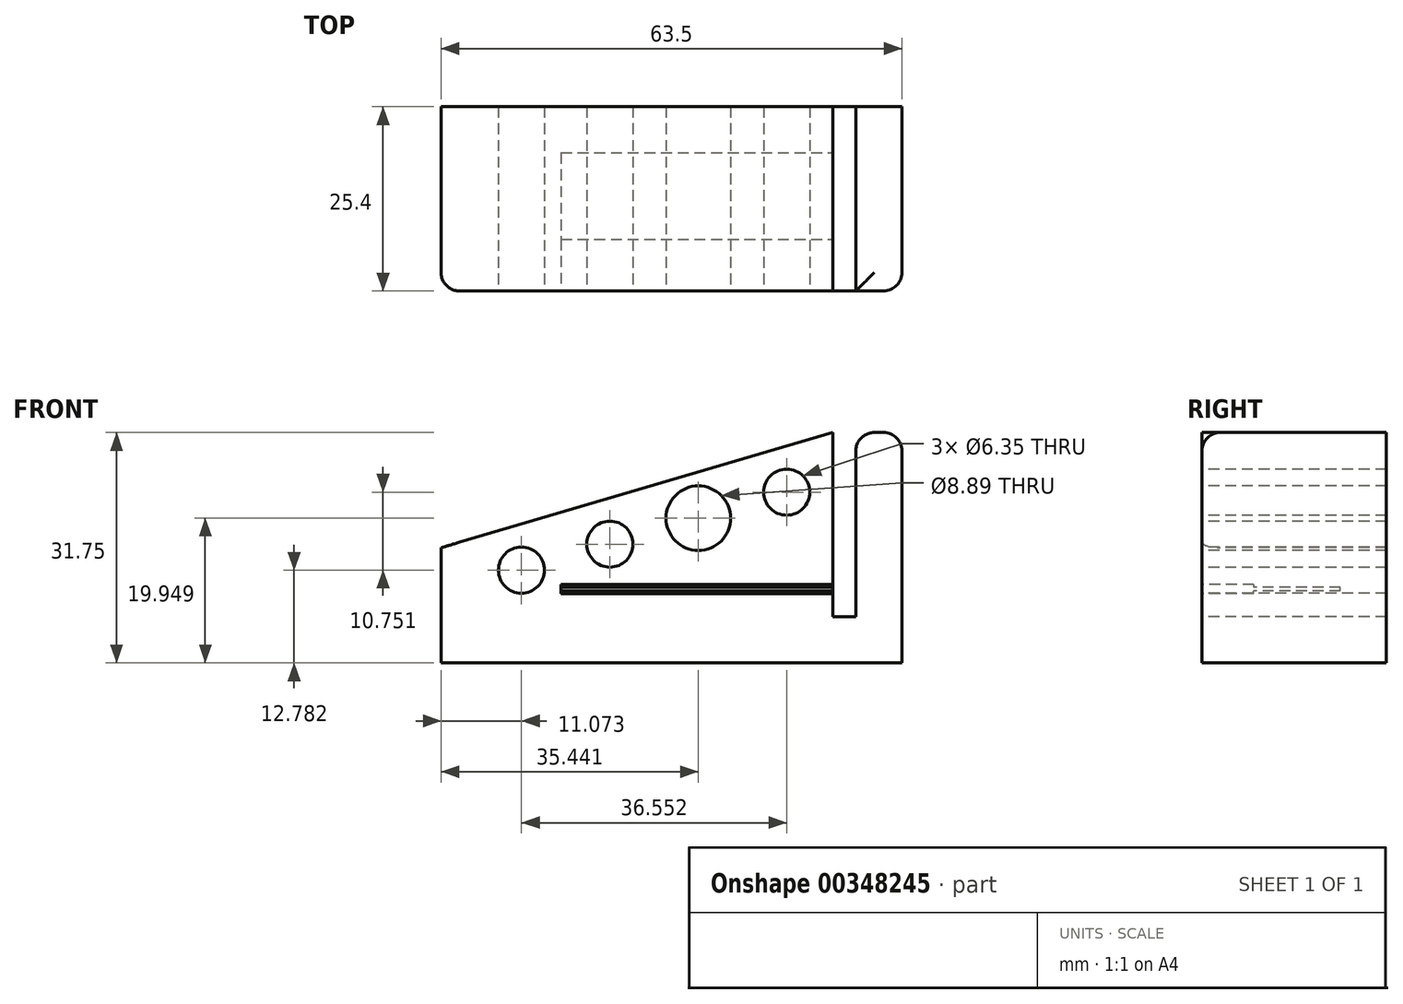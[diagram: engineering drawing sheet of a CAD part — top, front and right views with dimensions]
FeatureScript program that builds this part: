
annotation { "Feature Type Name" : "Feature", "Feature Type Description" : "" }
export const myFeature = defineFeature(function(context is Context, id is Id, definition is map)
    precondition{}
    {
        {
            var Q0;
            Q0=qCreatedBy(makeId("Top.planeOp"),FACE);
            var sketch = newSketch(context, id + "F0", { "sketchPlane" : qUnion([Q0])});
            skLineSegment(sketch, "E0.bottom", {"start": v(-31.75, 12.7) * mm, "end": v(31.75, 12.7) * mm});
            skLineSegment(sketch, "E0.top", {"start": v(-31.75, -12.7) * mm, "end": v(31.75, -12.7) * mm});
            skLineSegment(sketch, "E0.left", {"start": v(-31.75, 12.7) * mm, "end": v(-31.75, -12.7) * mm});
            skLineSegment(sketch, "E0.right", {"start": v(31.75, 12.7) * mm, "end": v(31.75, -12.7) * mm});
            skPoint(sketch, "E0.middle", {"position": v(0, 0) * mm});
            skSolve(sketch);
        }
        {
            var Q0;
            Q0 = qSketchRegion(id + "F0", true);
            extrude(context, id + "F1", {"entities" : qUnion([Q0]), "depth" : 50.8 * mm});
        }
        {
            var Q0;
            Q0=makeQuery(id+"F1.opExtrude","CAP_FACE",FACE,{"disambiguationData":[OSD([sQuery(id+"F0.wireOp",EDGE,"E0.bottom"),sQuery(id+"F0.wireOp",EDGE,"E0.top"),sQuery(id+"F0.wireOp",EDGE,"E0.left"),sQuery(id+"F0.wireOp",EDGE,"E0.right")])],"isStart":false});
            var sketch = newSketch(context, id + "F2", { "sketchPlane" : qUnion([Q0])});
            skLineSegment(sketch, "E1.bottom", {"start": v(22.23, 12.7) * mm, "end": v(25.4, 12.7) * mm});
            skLineSegment(sketch, "E1.top", {"start": v(22.22, -12.7) * mm, "end": v(25.4, -12.7) * mm});
            skLineSegment(sketch, "E1.left", {"start": v(22.22, 12.7) * mm, "end": v(22.22, -12.7) * mm});
            skLineSegment(sketch, "E1.right", {"start": v(25.4, 12.7) * mm, "end": v(25.4, -12.7) * mm});
            skLineSegment(sketch, "E2", {"start": v(23.81, 12.7) * mm, "end": v(22.23, 0) * mm, "construction": true});
            skSolve(sketch);
        }
        {
            var Q0;
            Q0 = qSketchRegion(id + "F2", true);
            extrude(context, id + "F3", {"entities" : qUnion([Q0]), "operationType" : NewBodyOperationType.REMOVE, "oppositeDirection" : true, "depth" : 25.4 * mm});
        }
        {
            var Q0;
            Q0=makeQuery(id+"F1.opExtrude","SWEPT_FACE",FACE,{"disambiguationData":[OSD([sQuery(id+"F0.wireOp",EDGE,"E0.top")])]});
            var sketch = newSketch(context, id + "F4", { "sketchPlane" : qUnion([Q0])});
            skLineSegment(sketch, "E3.bottom", {"start": v(-15.24, 29.85) * mm, "end": v(25.4, 29.85) * mm});
            skLineSegment(sketch, "E3.top", {"start": v(-15.24, 28.58) * mm, "end": v(25.4, 28.58) * mm});
            skLineSegment(sketch, "E3.left", {"start": v(-15.24, 29.84) * mm, "end": v(-15.24, 28.58) * mm});
            skLineSegment(sketch, "E3.right", {"start": v(25.4, 29.84) * mm, "end": v(25.4, 28.58) * mm});
            skLineSegment(sketch, "E4", {"start": v(5.08, 29.84) * mm, "end": v(-15.24, 29.21) * mm, "construction": true});
            skSolve(sketch);
        }
        {
            var Q0;
            Q0 = qSketchRegion(id + "F4", true);
            extrude(context, id + "F5", {"entities" : qUnion([Q0]), "operationType" : NewBodyOperationType.REMOVE, "oppositeDirection" : true, "depth" : 7.11 * mm});
        }
        {
            var Q0;
            Q0=makeQuery(id+"F1.opExtrude","SWEPT_FACE",FACE,{"disambiguationData":[OSD([sQuery(id+"F0.wireOp",EDGE,"E0.top")])]});
            var sketch = newSketch(context, id + "F6", { "sketchPlane" : qUnion([Q0])});
            skLineSegment(sketch, "E5.bottom", {"start": v(31.75, 19.05) * mm, "end": v(-31.75, 19.05) * mm});
            skLineSegment(sketch, "E5.top", {"start": v(31.75, 0) * mm, "end": v(-31.75, 0) * mm});
            skLineSegment(sketch, "E5.left", {"start": v(31.75, 19.05) * mm, "end": v(31.75, 0) * mm});
            skLineSegment(sketch, "E5.right", {"start": v(-31.75, 19.05) * mm, "end": v(-31.75, 0) * mm});
            skSolve(sketch);
        }
        {
            var Q0;
            Q0 = qSketchRegion(id + "F6", true);
            extrude(context, id + "F7", {"entities" : qUnion([Q0]), "operationType" : NewBodyOperationType.REMOVE, "oppositeDirection" : true, "depth" : 25.4 * mm});
        }
        {
            var Q0;
            Q0=makeQuery(id+"F1.opExtrude","SWEPT_FACE",FACE,{"disambiguationData":[OSD([sQuery(id+"F0.wireOp",EDGE,"E0.top")])]});
            var sketch = newSketch(context, id + "F8", { "sketchPlane" : qUnion([Q0])});
            skLineSegment(sketch, "E6", {"start": v(-31.75, 34.93) * mm, "end": v(22.23, 50.8) * mm});
            skLineSegment(sketch, "E7", {"start": v(22.23, 50.8) * mm, "end": v(-31.75, 50.8) * mm});
            skLineSegment(sketch, "E8", {"start": v(-31.75, 50.8) * mm, "end": v(-31.75, 34.93) * mm});
            skSolve(sketch);
        }
        {
            var Q0;
            Q0 = qSketchRegion(id + "F8", true);
            extrude(context, id + "F9", {"entities" : qUnion([Q0]), "operationType" : NewBodyOperationType.REMOVE, "oppositeDirection" : true, "depth" : 25.4 * mm});
        }
        {
            var Q0;
            Q0=makeQuery(id+"F5.boolean.opBoolean","COPY",FACE,{"derivedFrom":makeQuery(id+"F5.opExtrude","CAP_FACE",FACE,{"disambiguationData":[OSD([sQuery(id+"F4.wireOp",EDGE,"E3.bottom"),sQuery(id+"F4.wireOp",EDGE,"E3.top"),sQuery(id+"F4.wireOp",EDGE,"E3.left"),sQuery(id+"F4.wireOp",EDGE,"E3.right")])],"isStart":false})});
            var sketch = newSketch(context, id + "F10", { "sketchPlane" : qUnion([Q0])});
            skLineSegment(sketch, "E9.bottom", {"start": v(-15.24, 29.46) * mm, "end": v(22.22, 29.46) * mm});
            skLineSegment(sketch, "E9.top", {"start": v(-15.24, 28.96) * mm, "end": v(22.22, 28.96) * mm});
            skLineSegment(sketch, "E9.left", {"start": v(-15.24, 29.46) * mm, "end": v(-15.24, 28.96) * mm});
            skLineSegment(sketch, "E9.right", {"start": v(22.22, 29.46) * mm, "end": v(22.22, 28.96) * mm});
            skLineSegment(sketch, "E10", {"start": v(-15.24, 29.21) * mm, "end": v(-6.5, 29.21) * mm, "construction": true});
            skLineSegment(sketch, "E11", {"start": v(-15.24, 29.21) * mm, "end": v(-15.1, 29.21) * mm, "construction": true});
            skPoint(sketch, "E11.endSnap0", {"position": v(-15.24, 29.21) * mm});
            skSolve(sketch);
        }
        {
            var Q0;
            Q0 = qSketchRegion(id + "F10", true);
            extrude(context, id + "F11", {"entities" : qUnion([Q0]), "operationType" : NewBodyOperationType.REMOVE, "oppositeDirection" : true, "depth" : 11.94 * mm});
        }
        {
            var Q0;
            Q0=makeQuery(id+"F1.opExtrude","SWEPT_FACE",FACE,{"disambiguationData":[OSD([sQuery(id+"F0.wireOp",EDGE,"E0.top")])]});
            var sketch = newSketch(context, id + "F12", { "sketchPlane" : qUnion([Q0])});
            skCircle(sketch, "E12", {"center": v(15.87, 42.58) * mm, "radius": 3.18 * mm});
            skCircle(sketch, "E13", {"center": v(3.7, 39) * mm, "radius": 4.45 * mm});
            skCircle(sketch, "E14", {"center": v(-8.5, 35.42) * mm, "radius": 3.18 * mm});
            skCircle(sketch, "E15", {"center": v(-20.68, 31.83) * mm, "radius": 3.18 * mm});
            skLineSegment(sketch, "E16", {"start": v(-31.75, 28.58) * mm, "end": v(22.23, 44.45) * mm, "construction": true});
            skLineSegment(sketch, "E17", {"start": v(-20.68, 31.83) * mm, "end": v(-8.5, 35.42) * mm, "construction": true});
            skLineSegment(sketch, "E18", {"start": v(3.7, 39) * mm, "end": v(15.88, 42.58) * mm, "construction": true});
            skLineSegment(sketch, "E19", {"start": v(-8.5, 35.42) * mm, "end": v(3.7, 39) * mm, "construction": true});
            skSolve(sketch);
        }
        {
            var Q0;
            Q0 = qSketchRegion(id + "F12", true);
            extrude(context, id + "F13", {"entities" : qUnion([Q0]), "operationType" : NewBodyOperationType.REMOVE, "oppositeDirection" : true, "depth" : 25.4 * mm});
        }
        {
            var Q0;
            Q0=makeQuery(id+"F9.boolean.opBoolean","COPY",EDGE,{"derivedFrom":makeQuery(id+"F9.opExtrude","SWEPT_EDGE",EDGE,{"disambiguationData":[OSD([sQuery(id+"F0.wireOp",EDGE,"E0.top"),sQuery(id+"F0.wireOp",EDGE,"E0.left"),sQuery(id+"F8.wireOp",EDGE,"E6"),sQuery(id+"F8.wireOp",EDGE,"E8")])]})});
            var Q1;
            {var subQ0=sQuery(id+"F2.wireOp",EDGE,"E1.left");Q1=makeQuery(id+"F9.boolean.opBoolean","MERGE",EDGE,{"derivedFrom":[makeQuery(id+"F3.boolean.opBoolean","COPY",EDGE,{"derivedFrom":makeQuery(id+"F3.opExtrude","CAP_EDGE",EDGE,{"disambiguationData":[OSD([subQ0])],"isStart":true})}),makeQuery(id+"F9.opExtrude","SWEPT_EDGE",EDGE,{"disambiguationData":[OSD([sQuery(id+"F0.wireOp",EDGE,"E0.top"),sQuery(id+"F2.wireOp",EDGE,"E1.top"),subQ0,sQuery(id+"F8.wireOp",EDGE,"E6"),sQuery(id+"F8.wireOp",EDGE,"E7")])]})]});}
            var Q2;
            Q2=makeQuery(id+"F3.boolean.opBoolean","COPY",EDGE,{"derivedFrom":makeQuery(id+"F3.opExtrude","CAP_EDGE",EDGE,{"disambiguationData":[OSD([sQuery(id+"F2.wireOp",EDGE,"E1.right")])],"isStart":true})});
            var Q3;
            Q3=makeQuery(id+"F1.opExtrude","SWEPT_EDGE",EDGE,{"disambiguationData":[OSD([sQuery(id+"F0.wireOp",EDGE,"E0.top"),sQuery(id+"F0.wireOp",EDGE,"E0.right")])]});
            var Q4;
            Q4=makeQuery(id+"F3.boolean.opBoolean","COPY",EDGE,{"derivedFrom":makeQuery(id+"F3.opExtrude","SWEPT_EDGE",EDGE,{"disambiguationData":[OSD([sQuery(id+"F0.wireOp",EDGE,"E0.top"),sQuery(id+"F2.wireOp",EDGE,"E1.top"),sQuery(id+"F2.wireOp",EDGE,"E1.right")])]})});
            var Q5;
            {var subQ0=sQuery(id+"F0.wireOp",EDGE,"E0.top");var subQ1=sQuery(id+"F2.wireOp",EDGE,"E1.left");Q5=makeQuery(id+"F5.boolean.opBoolean","SPLIT",EDGE,{"disambiguationData":[TD([makeQuery(id+"F5.opExtrude","SWEPT_FACE",FACE,{"disambiguationData":[OSD([sQuery(id+"F4.wireOp",EDGE,"E3.bottom")])]})])],"derivedFrom":makeQuery(id+"F3.boolean.opBoolean","COPY",EDGE,{"derivedFrom":makeQuery(id+"F3.opExtrude","SWEPT_EDGE",EDGE,{"disambiguationData":[OSD([subQ0,sQuery(id+"F2.wireOp",EDGE,"E1.top"),subQ1])]})})});}
            var Q6;
            {var subQ0=sQuery(id+"F0.wireOp",EDGE,"E0.top");var subQ1=sQuery(id+"F2.wireOp",EDGE,"E1.left");var subQ2=sQuery(id+"F2.wireOp",EDGE,"E1.top");Q6=makeQuery(id+"F5.boolean.opBoolean","SPLIT",EDGE,{"disambiguationData":[TD([makeQuery(id+"F5.opExtrude","SWEPT_FACE",FACE,{"disambiguationData":[OSD([sQuery(id+"F4.wireOp",EDGE,"E3.top")])]})])],"derivedFrom":makeQuery(id+"F3.boolean.opBoolean","COPY",EDGE,{"derivedFrom":makeQuery(id+"F3.opExtrude","SWEPT_EDGE",EDGE,{"disambiguationData":[OSD([subQ0,subQ2,subQ1])]})})});}
            var Q7;
            Q7=makeQuery(id+"F9.boolean.opBoolean","COPY",EDGE,{"derivedFrom":makeQuery(id+"F9.opExtrude","CAP_EDGE",EDGE,{"disambiguationData":[OSD([sQuery(id+"F8.wireOp",EDGE,"E6")])],"isStart":true})});
            var Q8;
            Q8=makeQuery(id+"F13.boolean.opBoolean","COPY",EDGE,{"derivedFrom":makeQuery(id+"F13.opExtrude","CAP_EDGE",EDGE,{"disambiguationData":[OSD([sQuery(id+"F12.wireOp",EDGE,"E15")])],"isStart":true})});
            var Q9;
            Q9=makeQuery(id+"F13.boolean.opBoolean","COPY",EDGE,{"derivedFrom":makeQuery(id+"F13.opExtrude","CAP_EDGE",EDGE,{"disambiguationData":[OSD([sQuery(id+"F12.wireOp",EDGE,"E14")])],"isStart":true})});
            var Q10;
            Q10=makeQuery(id+"F13.boolean.opBoolean","COPY",EDGE,{"derivedFrom":makeQuery(id+"F13.opExtrude","CAP_EDGE",EDGE,{"disambiguationData":[OSD([sQuery(id+"F12.wireOp",EDGE,"E13")])],"isStart":true})});
            var Q11;
            Q11=makeQuery(id+"F13.boolean.opBoolean","COPY",EDGE,{"derivedFrom":makeQuery(id+"F13.opExtrude","CAP_EDGE",EDGE,{"disambiguationData":[OSD([sQuery(id+"F12.wireOp",EDGE,"E12")])],"isStart":true})});
            var Q12;
            Q12=makeQuery(id+"F1.opExtrude","CAP_EDGE",EDGE,{"disambiguationData":[OSD([sQuery(id+"F0.wireOp",EDGE,"E0.right")])],"isStart":false});
            var Q13;
            Q13=makeQuery(id+"F3.boolean.opBoolean","COPY",EDGE,{"derivedFrom":makeQuery(id+"F3.opExtrude","CAP_EDGE",EDGE,{"disambiguationData":[OSD([sQuery(id+"F2.wireOp",EDGE,"E1.top")])],"isStart":false})});
            var Q14;
            Q14=makeQuery(id+"F7.boolean.opBoolean","COPY",EDGE,{"derivedFrom":makeQuery(id+"F7.opExtrude","CAP_EDGE",EDGE,{"disambiguationData":[OSD([sQuery(id+"F6.wireOp",EDGE,"E5.bottom")])],"isStart":true})});
            var Q15;
            Q15=makeQuery(id+"F1.opExtrude","SWEPT_EDGE",EDGE,{"disambiguationData":[OSD([sQuery(id+"F0.wireOp",EDGE,"E0.top"),sQuery(id+"F0.wireOp",EDGE,"E0.left")])]});
            var Q16;
            Q16=makeQuery(id+"F7.boolean.opBoolean","COPY",EDGE,{"derivedFrom":makeQuery(id+"F7.opExtrude","SWEPT_EDGE",EDGE,{"disambiguationData":[OSD([sQuery(id+"F0.wireOp",EDGE,"E0.top"),sQuery(id+"F0.wireOp",EDGE,"E0.left"),sQuery(id+"F6.wireOp",EDGE,"E5.bottom"),sQuery(id+"F6.wireOp",EDGE,"E5.right")])]})});
            var Q17;
            {var subQ0=sQuery(id+"F0.wireOp",EDGE,"E0.right");var subQ1=sQuery(id+"F0.wireOp",EDGE,"E0.top");Q17=makeQuery(id+"F3.boolean.opBoolean","SPLIT",EDGE,{"disambiguationData":[TD([makeQuery(id+"F1.opExtrude","SWEPT_FACE",FACE,{"disambiguationData":[OSD([subQ0])]})])],"derivedFrom":makeQuery(id+"F1.opExtrude","CAP_EDGE",EDGE,{"disambiguationData":[OSD([subQ1])],"isStart":false})});}
            var Q18;
            Q18=makeQuery(id+"F7.boolean.opBoolean","COPY",EDGE,{"derivedFrom":makeQuery(id+"F7.opExtrude","SWEPT_EDGE",EDGE,{"disambiguationData":[OSD([sQuery(id+"F0.wireOp",EDGE,"E0.top"),sQuery(id+"F0.wireOp",EDGE,"E0.right"),sQuery(id+"F6.wireOp",EDGE,"E5.bottom"),sQuery(id+"F6.wireOp",EDGE,"E5.left")])]})});
            fillet(context, id + "F14", {"entities" : qUnion([Q0, Q1, Q2, Q3, Q4, Q5, Q6, Q7, Q8, Q9, Q10, Q11, Q12, Q13, Q14, Q15, Q16, Q17, Q18]), "radius" : 2.54 * mm, "tangentPropagation" : true, "allowEdgeOverflow" : false});
        }
    });
